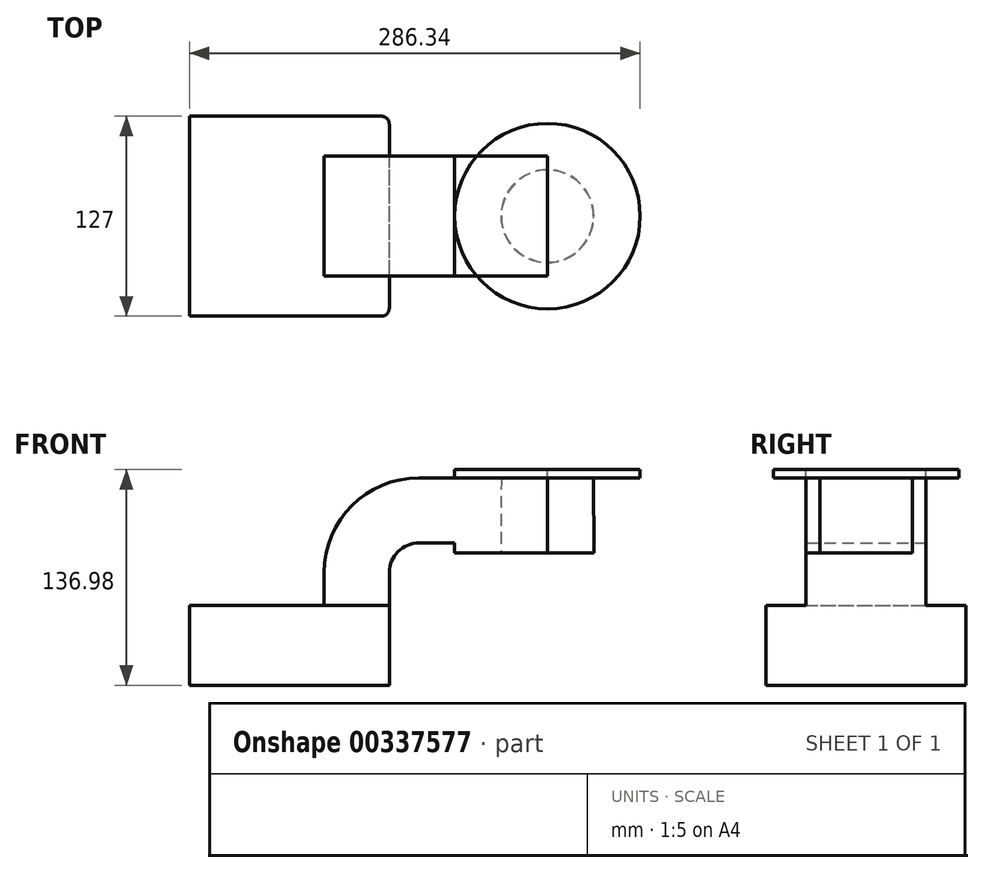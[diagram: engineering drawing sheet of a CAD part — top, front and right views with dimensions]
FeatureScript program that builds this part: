
annotation { "Feature Type Name" : "Feature", "Feature Type Description" : "" }
export const myFeature = defineFeature(function(context is Context, id is Id, definition is map)
    precondition{}
    {
        {
            var Q0;
            Q0=qCreatedBy(makeId("Front.planeOp"),FACE);
            var sketch = newSketch(context, id + "F0", { "sketchPlane" : qUnion([Q0])});
            skLineSegment(sketch, "E0.bottom", {"start": v(63.5, -25.4) * mm, "end": v(-63.5, -25.4) * mm});
            skLineSegment(sketch, "E0.top", {"start": v(63.5, 25.4) * mm, "end": v(-63.5, 25.4) * mm});
            skLineSegment(sketch, "E0.left", {"start": v(63.5, -25.4) * mm, "end": v(63.5, 25.4) * mm});
            skLineSegment(sketch, "E0.right", {"start": v(-63.5, -25.4) * mm, "end": v(-63.5, 25.4) * mm});
            skPoint(sketch, "E0.middle", {"position": v(0, 0) * mm});
            skLineSegment(sketch, "E1.bottom", {"start": v(163.92, 58.75) * mm, "end": v(104.99, 58.75) * mm});
            skLineSegment(sketch, "E1.top", {"start": v(163.92, 111.58) * mm, "end": v(104.99, 111.58) * mm});
            skLineSegment(sketch, "E1.left", {"start": v(163.92, 58.75) * mm, "end": v(163.92, 111.58) * mm});
            skLineSegment(sketch, "E1.right", {"start": v(104.99, 58.75) * mm, "end": v(104.99, 111.58) * mm});
            skPoint(sketch, "E1.middle", {"position": v(134.45, 85.17) * mm});
            skLineSegment(sketch, "E2", {"start": v(63.5, 25.4) * mm, "end": v(63.5, 46.15) * mm});
            skArc(sketch, "E3", {"start": v(63.5, 46.15) * mm, "mid": v(69.02, 59.47) * mm, "end": v(82.34, 65) * mm});
            skLineSegment(sketch, "E4", {"start": v(82.34, 65) * mm, "end": v(134.45, 65) * mm});
            skPoint(sketch, "E4.endSnap0", {"position": v(134.45, 58.75) * mm});
            skLineSegment(sketch, "E5.0", {"start": v(82.34, 106.4) * mm, "end": v(134.62, 106.4) * mm});
            skArc(sketch, "E5.1", {"start": v(22.1, 46.15) * mm, "mid": v(39.74, 88.75) * mm, "end": v(82.34, 106.4) * mm});
            skLineSegment(sketch, "E5.2", {"start": v(22.1, 25.4) * mm, "end": v(22.1, 46.15) * mm});
            skLineSegment(sketch, "E6", {"start": v(134.45, 58.75) * mm, "end": v(134.62, 106.4) * mm});
            skFitSpline(sketch, "E7", {"points": [v(-63.5, 25.4) * mm, v(82.34, 106.4) * mm], "startDerivative": vector(80.06, 154.05) * mm, "endDerivative": vector(212.29, -1.96) * mm});
            skSolve(sketch);
        }
        {
            var Q0;
            Q0=makeQuery(id+"F0.imprint","IMPRINT",FACE,{"disambiguationData":[TD([[makeQuery(id+"F0.imprint","IMPRINT",EDGE,{"derivedFrom":sQuery(id+"F0.wireOp",EDGE,"E0.bottom")}),-1.0]])]});
            var Q1;
            Q1=sQuery(id+"F0.wireOp",EDGE,"E0.top");
            extrude(context, id + "F1", {"entities" : qUnion([Q0]), "surfaceEntities" : qUnion([Q1]), "endBound" : BoundingType.SYMMETRIC, "depth" : 127 * mm});
        }
        {
            var Q0;
            {var subQ1=sQuery(id+"F0.wireOp",EDGE,"E2");Q0=makeQuery(id+"F0.imprint","IMPRINT",FACE,{"disambiguationData":[TD([[makeQuery(id+"F0.imprint","IMPRINT",EDGE,{"derivedFrom":subQ1}),1.0]])]});}
            extrude(context, id + "F2", {"entities" : qUnion([Q0]), "operationType" : NewBodyOperationType.ADD, "endBound" : BoundingType.SYMMETRIC, "depth" : 76.2 * mm});
        }
        {
            var Q0;
            {var subQ0=sQuery(id+"F0.wireOp",EDGE,"E1.right");var subQ1=sQuery(id+"F0.wireOp",EDGE,"E1.top");var subQ2=makeQuery(id+"F0.imprint","INTERSECT",VERTEX,{"derivedFrom":[subQ1,subQ0]});Q0=makeQuery(id+"F0.imprint","IMPRINT",FACE,{"disambiguationData":[TD([[makeQuery(id+"F0.imprint","IMPRINT",EDGE,{"disambiguationData":[TD([[subQ2,1.0]])],"derivedFrom":subQ1}),1.0]])]});}
            var Q1;
            {var subQ0=sQuery(id+"F0.wireOp",EDGE,"E1.left");Q1=makeQuery(id+"F0.imprint","IMPRINT",FACE,{"disambiguationData":[TD([[makeQuery(id+"F0.imprint","IMPRINT",EDGE,{"derivedFrom":subQ0}),1.0]])]});}
            var Q2;
            {var subQ0=sQuery(id+"F0.wireOp",EDGE,"E1.right");var subQ1=sQuery(id+"F0.wireOp",EDGE,"E1.bottom");var subQ2=makeQuery(id+"F0.imprint","INTERSECT",VERTEX,{"derivedFrom":[subQ1,subQ0]});Q2=makeQuery(id+"F0.imprint","IMPRINT",FACE,{"disambiguationData":[TD([[makeQuery(id+"F0.imprint","IMPRINT",EDGE,{"disambiguationData":[TD([[subQ2,1.0]])],"derivedFrom":subQ1}),-1.0]])]});}
            var Q3;
            {var subQ0=sQuery(id+"F0.wireOp",EDGE,"E4");var subQ1=sQuery(id+"F0.wireOp",EDGE,"E1.right");var subQ2=makeQuery(id+"F0.imprint","INTERSECT",VERTEX,{"derivedFrom":[subQ1,subQ0]});Q3=makeQuery(id+"F0.imprint","IMPRINT",FACE,{"disambiguationData":[TD([[makeQuery(id+"F0.imprint","IMPRINT",EDGE,{"disambiguationData":[TD([[subQ2,-1.0]])],"derivedFrom":subQ1}),-1.0]])]});}
            extrude(context, id + "F3", {"entities" : qUnion([Q0, Q1, Q2, Q3]), "operationType" : NewBodyOperationType.ADD, "endBound" : BoundingType.SYMMETRIC, "depth" : 76.2 * mm});
        }
        {
            var Q0;
            {var subQ4=sQuery(id+"F0.wireOp",EDGE,"E5.1");Q0=makeQuery(id+"F0.imprint","IMPRINT",FACE,{"disambiguationData":[TD([[makeQuery(id+"F0.imprint","IMPRINT",EDGE,{"derivedFrom":subQ4}),1.0]])]});}
            extrude(context, id + "F4", {"entities" : qUnion([Q0]), "operationType" : NewBodyOperationType.ADD, "endBound" : BoundingType.SYMMETRIC, "depth" : 50.8 * mm});
        }
        {
            var Q0;
            {var subQ1=sQuery(id+"F0.wireOp",EDGE,"E1.top");Q0=makeQuery(id+"F0.imprint","IMPRINT",FACE,{"disambiguationData":[TD([[makeQuery(id+"F0.imprint","IMPRINT",EDGE,{"derivedFrom":subQ1}),1.0]])]});}
            var Q1;
            Q1=sQuery(id+"F0.wireOp",EDGE,"E1.left");
            revolve(context, id + "F5", {"entities" : qUnion([Q0]), "axis" : qUnion([Q1]), "revolveType" : RevolveType.FULL});
        }
        {
            var Q0;
            Q0=makeQuery(id+"F1.opExtrude","CAP_EDGE",EDGE,{"disambiguationData":[OSD([sQuery(id+"F0.wireOp",EDGE,"E0.left")])],"isStart":false});
            var Q1;
            Q1=makeQuery(id+"F1.opExtrude","CAP_EDGE",EDGE,{"disambiguationData":[OSD([sQuery(id+"F0.wireOp",EDGE,"E0.left")])],"isStart":true});
            fillet(context, id + "F6", {"entities" : qUnion([Q0, Q1]), "radius" : 5.08 * mm, "tangentPropagation" : true, "allowEdgeOverflow" : false});
        }
    });
